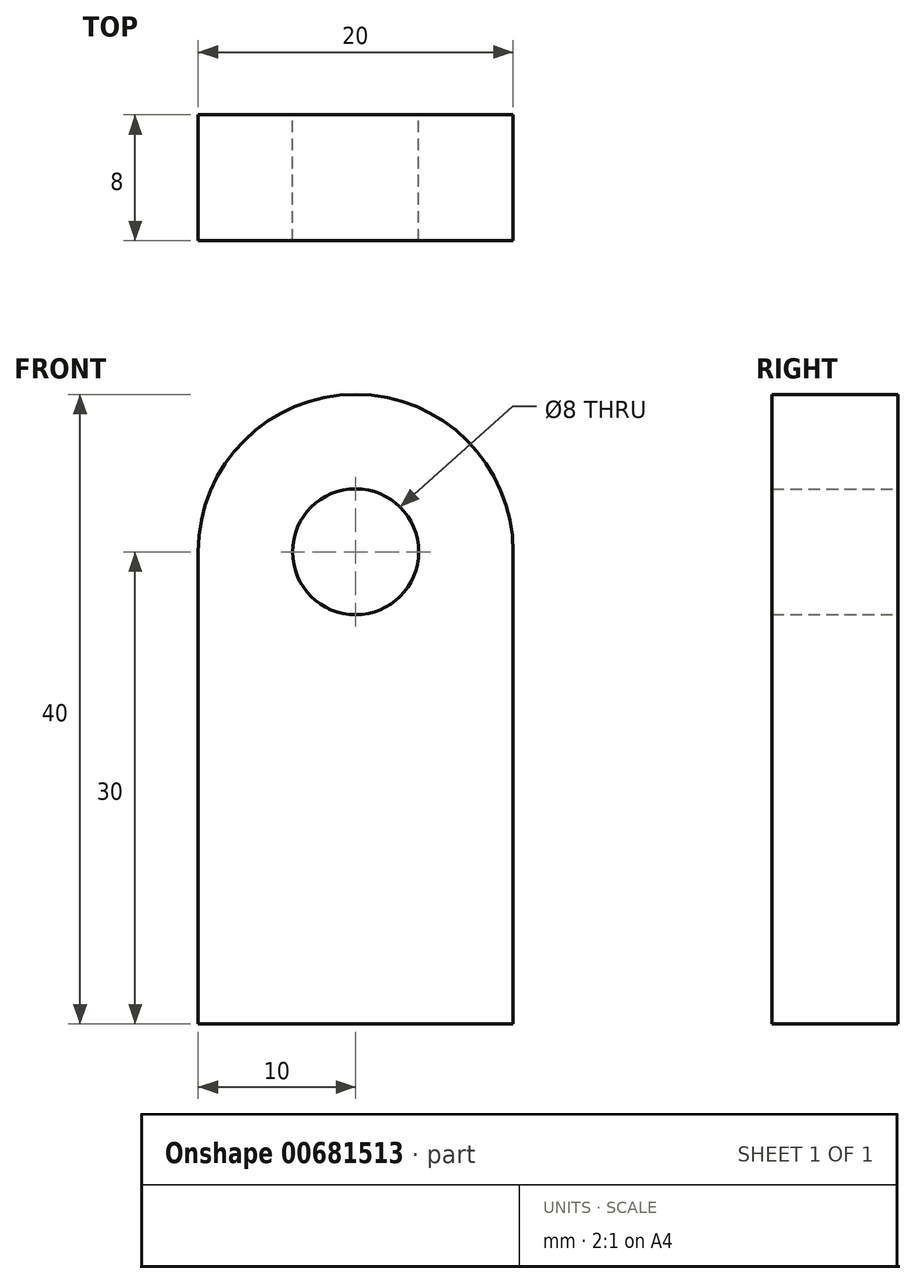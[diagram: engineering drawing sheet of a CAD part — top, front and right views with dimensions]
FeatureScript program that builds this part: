
annotation { "Feature Type Name" : "Feature", "Feature Type Description" : "" }
export const myFeature = defineFeature(function(context is Context, id is Id, definition is map)
    precondition{}
    {
        {
            var Q0;
            Q0=qCreatedBy(makeId("Front.planeOp"),FACE);
            var sketch = newSketch(context, id + "F0", { "sketchPlane" : qUnion([Q0])});
            skLineSegment(sketch, "E0.bottom", {"start": v(-10, 0) * mm, "end": v(10, 0) * mm});
            skLineSegment(sketch, "E0.left", {"start": v(-10, 0) * mm, "end": v(-10, 30) * mm});
            skLineSegment(sketch, "E0.right", {"start": v(10, 0) * mm, "end": v(10, 30) * mm});
            skCircle(sketch, "E1", {"center": v(0, 30) * mm, "radius": 4 * mm});
            skArc(sketch, "E2", {"start": v(10, 30) * mm, "mid": v(0, 40) * mm, "end": v(-10, 30) * mm});
            skSolve(sketch);
        }
        {
            var Q0;
            Q0 = qSketchRegion(id + "F0", true);
            extrude(context, id + "F1", {"entities" : qUnion([Q0]), "endBound" : BoundingType.SYMMETRIC, "depth" : 8 * mm, "offsetDistance" : 25 * mm});
        }
    });
